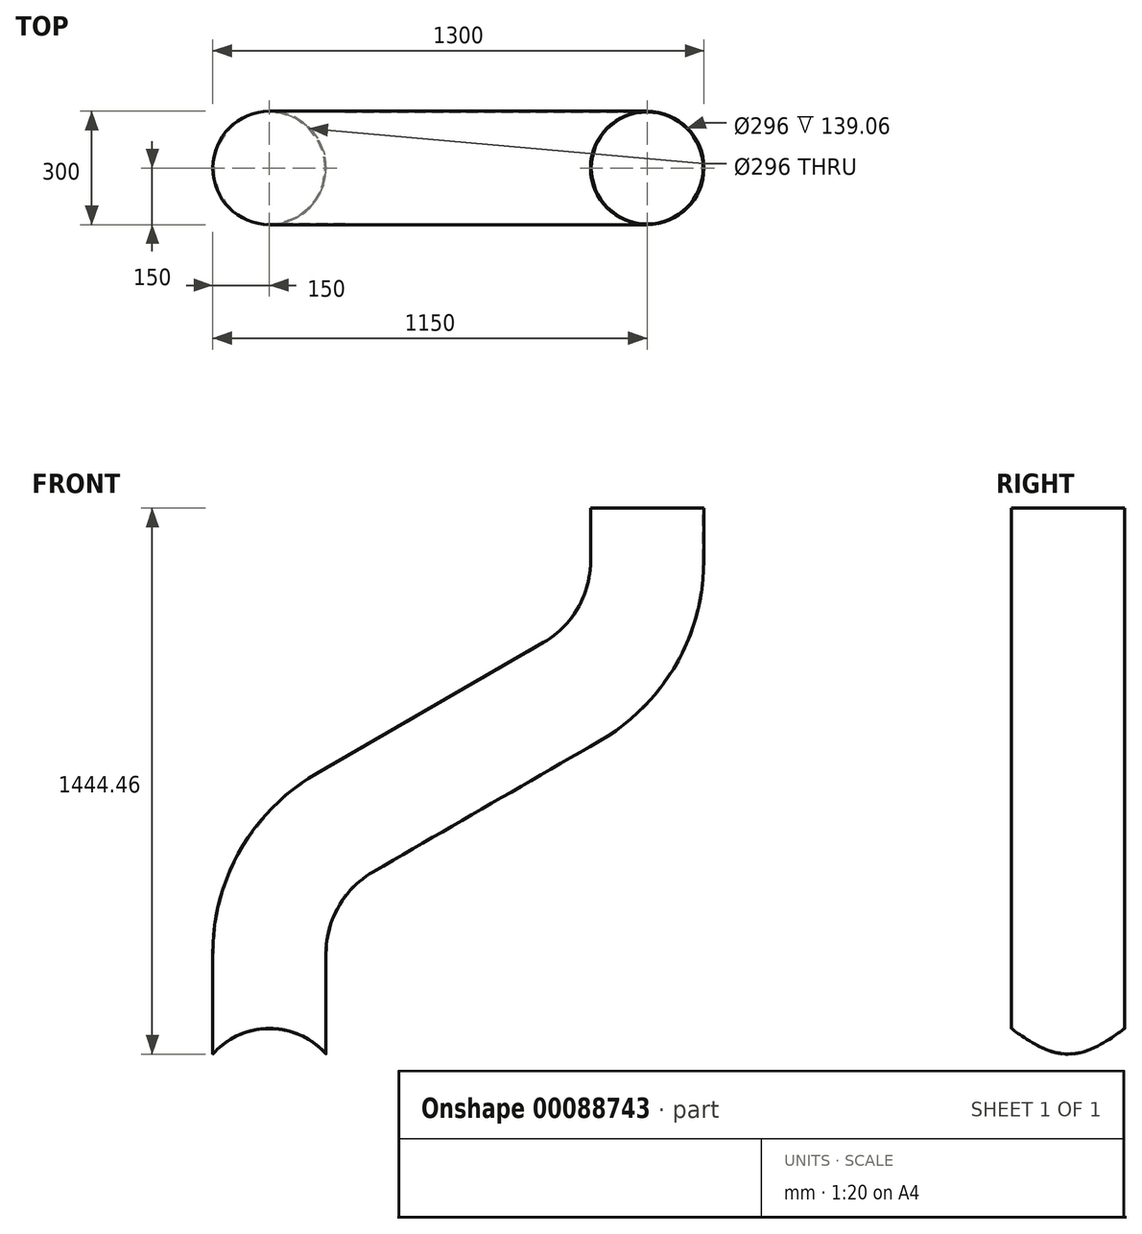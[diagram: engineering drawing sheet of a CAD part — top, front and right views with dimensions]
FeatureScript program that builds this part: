
annotation { "Feature Type Name" : "Feature", "Feature Type Description" : "" }
export const myFeature = defineFeature(function(context is Context, id is Id, definition is map)
    precondition{}
    {
        {
            var Q0;
            Q0=qCreatedBy(makeId("Front.planeOp"),FACE);
            var sketch = newSketch(context, id + "F0", { "sketchPlane" : qUnion([Q0])});
            skLineSegment(sketch, "E0", {"start": v(0, 0) * mm, "end": v(0, 398.46) * mm});
            skLineSegment(sketch, "E1", {"start": v(200, 744.87) * mm, "end": v(800, 1091.28) * mm});
            skLineSegment(sketch, "E2", {"start": v(1000, 1437.69) * mm, "end": v(1000, 1576.75) * mm});
            skPoint(sketch, "E3.visualSharp", {"position": v(0, 629.4) * mm});
            skArc(sketch, "E3.filletArc", {"start": v(200, 744.87) * mm, "mid": v(53.59, 598.46) * mm, "end": v(0, 398.46) * mm});
            skPoint(sketch, "E4.visualSharp", {"position": v(1000, 1206.75) * mm});
            skArc(sketch, "E4.filletArc", {"start": v(800, 1091.28) * mm, "mid": v(946.41, 1237.69) * mm, "end": v(1000, 1437.69) * mm});
            skCircle(sketch, "E5", {"center": v(0, 0) * mm, "radius": 200 * mm});
            skLineSegment(sketch, "E6", {"start": v(-152.5, 129.4) * mm, "end": v(152.5, 129.4) * mm});
            skSolve(sketch);
        }
        {
            var Q0;
            Q0=qCreatedBy(makeId("Top.planeOp"),FACE);
            var sketch = newSketch(context, id + "F1", { "sketchPlane" : qUnion([Q0])});
            skCircle(sketch, "E7", {"center": v(0, 0) * mm, "radius": 150 * mm});
            skCircle(sketch, "E8", {"center": v(0, 0) * mm, "radius": 148 * mm});
            skSolve(sketch);
        }
        {
            var Q0;
            Q0=makeQuery(id+"F1.imprint","IMPRINT",FACE,{"disambiguationData":[TD([[makeQuery(id+"F1.imprint","IMPRINT",EDGE,{"derivedFrom":sQuery(id+"F1.wireOp",EDGE,"E7")}),1.0]])]});
            var Q1;
            Q1=sQuery(id+"F0.wireOp",EDGE,"E0");
            var Q2;
            Q2=sQuery(id+"F0.wireOp",EDGE,"E3.filletArc");
            var Q3;
            Q3=sQuery(id+"F0.wireOp",EDGE,"E1");
            var Q4;
            Q4=sQuery(id+"F0.wireOp",EDGE,"E4.filletArc");
            var Q5;
            Q5=sQuery(id+"F0.wireOp",EDGE,"E2");
            sweep(context, id + "F2", {"profiles" : qUnion([Q0]), "path" : qUnion([Q1, Q2, Q3, Q4, Q5])});
        }
        {
            var Q0;
            Q0 = qSketchRegion(id + "F0", true);
            extrude(context, id + "F3", {"entities" : qUnion([Q0]), "operationType" : NewBodyOperationType.REMOVE, "endBound" : BoundingType.THROUGH_ALL, "oppositeDirection" : true, "depth" : 25 * mm, "hasSecondDirection" : true, "secondDirectionBound" : BoundingType.THROUGH_ALL, "secondDirectionOppositeDirection" : false, "secondDirectionDepth" : 25 * mm});
        }
    });
